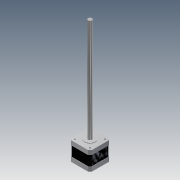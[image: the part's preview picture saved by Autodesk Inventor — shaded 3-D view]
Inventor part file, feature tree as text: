
AUTODESK INVENTOR PART (.ipt)
format: ipt  version: 2014 (Build 180170000, 170)  size: 166,400 bytes
history: native  units: mm
features: extrude x5, sketch x5, chamfer x1, projected_geometry x1
ambient origin geometry x8: Origin, YZ Plane, XZ Plane, XY Plane, X Axis, Y Axis, Z Axis, Center Point
bodies: Solid1 (feature_tree)
feature tree (12):
  extrude  "Extrusion1"  Depth=42.3mm
  chamfer  "Chamfer1"  Distance=9.0mm
  extrude  "Extrusion2"  Depth=0.5mm
  extrude  "Extrusion3"  Depth=0.5mm
  extrude  "Extrusion4"  Depth=20.0mm TaperAngle=0.0deg
  extrude  "Extrusion5"  Depth=9.0mm TaperAngle=0.0deg
  sketch  "Sketch1"  dims[d0=42.3mm d1=31.0mm]
  sketch  "Sketch3"  dims[d2=3.0mm d3=9.0mm d4=0.0mm]
  projected_geometry  "Projected Loop1"
  sketch  "Sketch4"  dims[d5=4.0mm d6=2.0mm d7=45.0deg d8=0.5mm]
  sketch  "Sketch5"  dims[d10=0.5mm d11=0.5mm]
  sketch  "Sketch6"  dims[d12=0.5mm d13=20.0mm d14=0.0mm d15=9.0mm d16=0.0mm d17=22.0mm d18=1.0mm d19=0.0mm d20=8.0mm d21=210.0mm d22=0.0mm]
